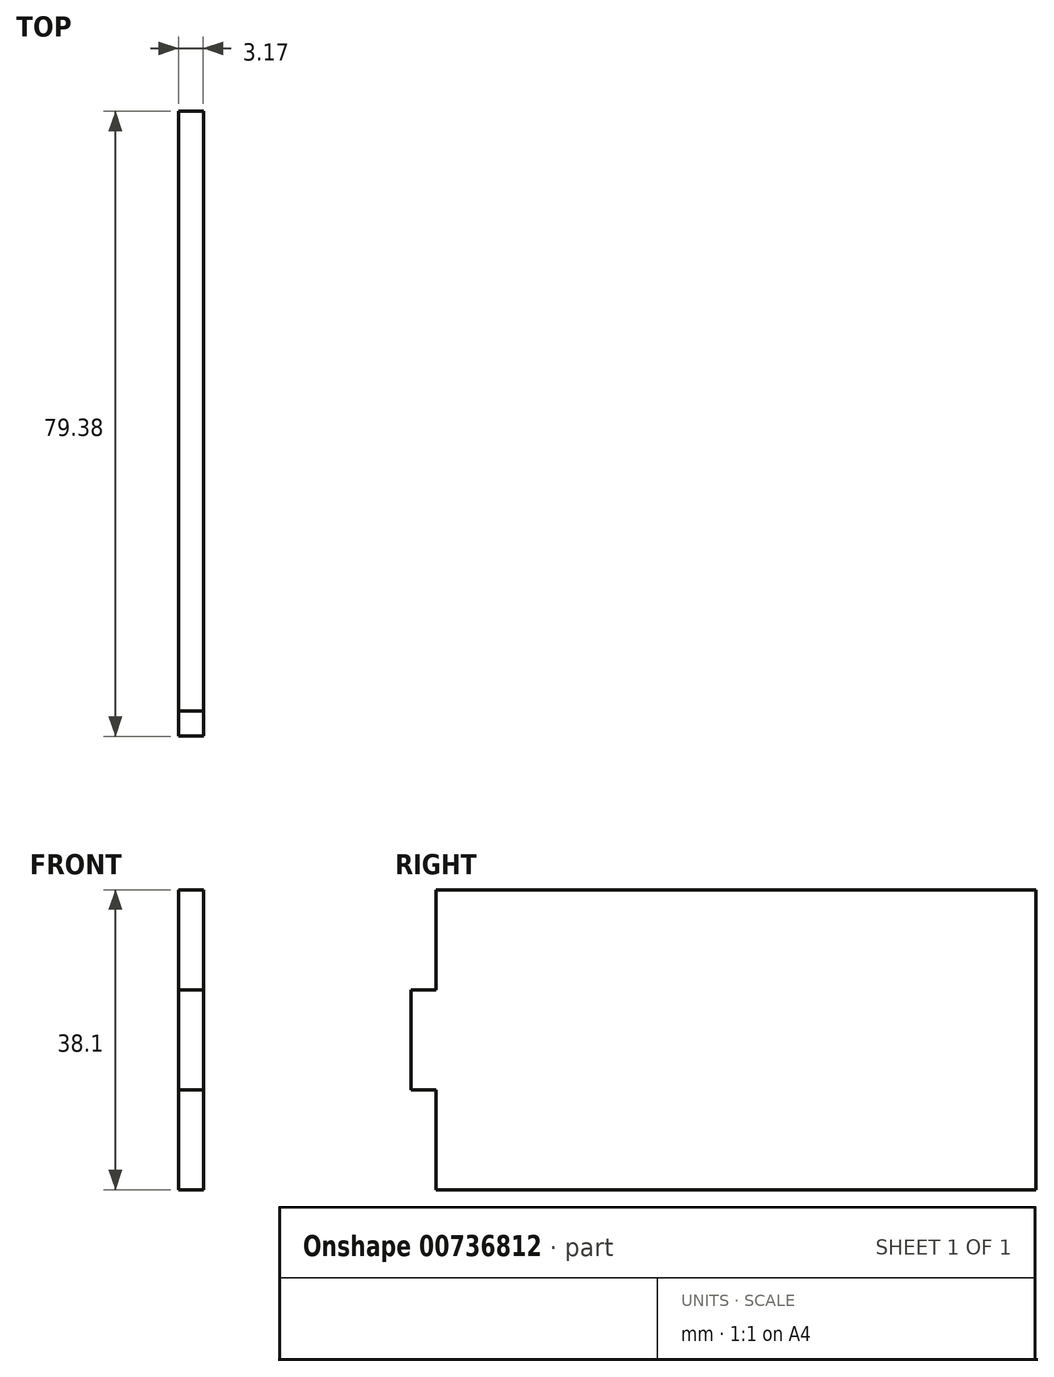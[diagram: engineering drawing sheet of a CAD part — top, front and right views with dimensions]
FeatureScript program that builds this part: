
annotation { "Feature Type Name" : "Feature", "Feature Type Description" : "" }
export const myFeature = defineFeature(function(context is Context, id is Id, definition is map)
    precondition{}
    {
        {
            var Q0;
            Q0=qCreatedBy(makeId("Right.planeOp"),FACE);
            var sketch = newSketch(context, id + "F0", { "sketchPlane" : qUnion([Q0])});
            skLineSegment(sketch, "E0.top", {"start": v(0, 38.1) * mm, "end": v(-76.2, 38.1) * mm});
            skLineSegment(sketch, "E0.right", {"start": v(-76.2, 0) * mm, "end": v(-76.2, 38.1) * mm});
            skLineSegment(sketch, "E1", {"start": v(-76.2, 0) * mm, "end": v(0, 0) * mm});
            skLineSegment(sketch, "E2", {"start": v(0, 0) * mm, "end": v(0, 38.1) * mm});
            skLineSegment(sketch, "E3.bottom", {"start": v(-76.2, 12.7) * mm, "end": v(-79.38, 12.7) * mm});
            skLineSegment(sketch, "E3.top", {"start": v(-76.2, 25.4) * mm, "end": v(-79.38, 25.4) * mm});
            skLineSegment(sketch, "E3.left", {"start": v(-76.2, 12.7) * mm, "end": v(-76.2, 25.4) * mm});
            skLineSegment(sketch, "E3.right", {"start": v(-79.38, 12.7) * mm, "end": v(-79.38, 25.4) * mm});
            skSolve(sketch);
        }
        {
            var Q0;
            Q0=makeQuery(id+"F0.imprint","IMPRINT",FACE,{"disambiguationData":[TD([[makeQuery(id+"F0.imprint","IMPRINT",EDGE,{"derivedFrom":sQuery(id+"F0.wireOp",EDGE,"E3.bottom")}),-1.0]])]});
            var Q1;
            {var subQ2=sQuery(id+"F0.wireOp",EDGE,"E0.top");Q1=makeQuery(id+"F0.imprint","IMPRINT",FACE,{"disambiguationData":[TD([[makeQuery(id+"F0.imprint","IMPRINT",EDGE,{"derivedFrom":subQ2}),1.0]])]});}
            extrude(context, id + "F1", {"entities" : qUnion([Q0, Q1]), "depth" : 3.17 * mm, "offsetDistance" : 25.4 * mm});
        }
    });
